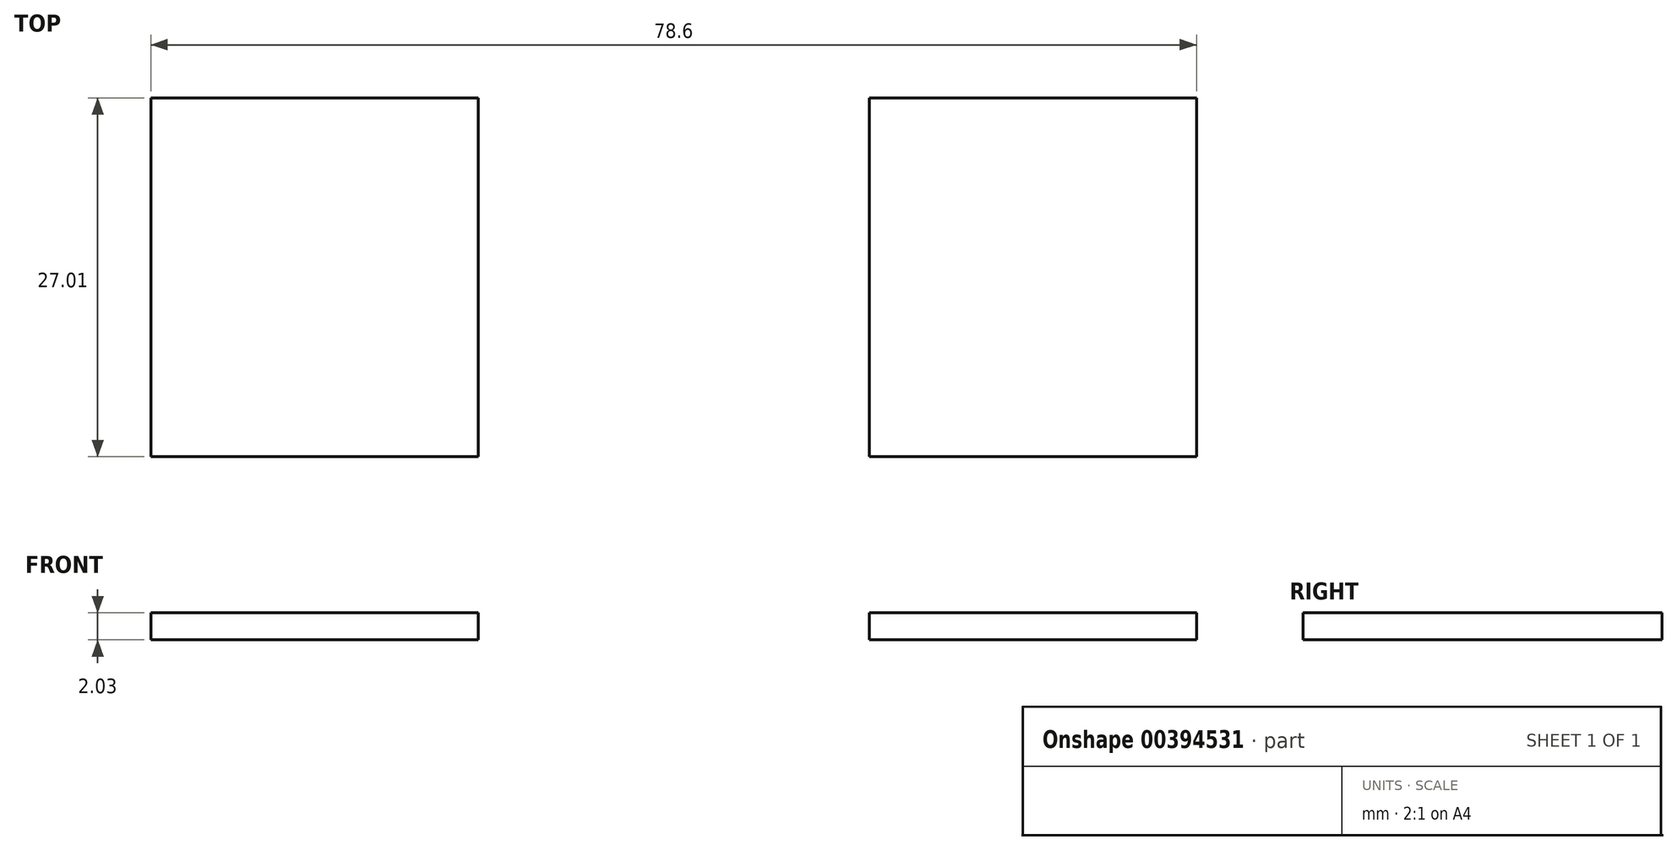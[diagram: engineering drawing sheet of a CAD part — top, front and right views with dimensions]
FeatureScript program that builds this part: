
annotation { "Feature Type Name" : "Feature", "Feature Type Description" : "" }
export const myFeature = defineFeature(function(context is Context, id is Id, definition is map)
    precondition{}
    {
        {
            var Q0;
            Q0=qCreatedBy(makeId("Top.planeOp"),FACE);
            var sketch = newSketch(context, id + "F0", { "sketchPlane" : qUnion([Q0])});
            skLineSegment(sketch, "E0.bottom", {"start": v(-39.3, 27) * mm, "end": v(-14.71, 27) * mm});
            skLineSegment(sketch, "E0.top", {"start": v(-39.3, 0) * mm, "end": v(-14.71, 0) * mm});
            skLineSegment(sketch, "E0.left", {"start": v(-39.3, 27) * mm, "end": v(-39.3, 0) * mm});
            skLineSegment(sketch, "E0.right", {"start": v(-14.71, 27) * mm, "end": v(-14.71, 0) * mm});
            skLineSegment(sketch, "E1.MirrorCS", {"start": v(14.71, 27) * mm, "end": v(14.71, 0) * mm});
            skLineSegment(sketch, "E2.MirrorCS", {"start": v(39.3, 27) * mm, "end": v(39.3, 0) * mm});
            skLineSegment(sketch, "E3.MirrorCS", {"start": v(39.3, 0) * mm, "end": v(14.71, 0) * mm});
            skLineSegment(sketch, "E4.MirrorCS", {"start": v(39.3, 27) * mm, "end": v(14.71, 27) * mm});
            skLineSegment(sketch, "E5.bottom", {"start": v(-8.26, 0.2) * mm, "end": v(9.47, 0.2) * mm});
            skLineSegment(sketch, "E5.top", {"start": v(-8.26, -13.9) * mm, "end": v(9.47, -13.9) * mm});
            skLineSegment(sketch, "E5.left", {"start": v(-8.26, 0.2) * mm, "end": v(-8.26, -13.9) * mm});
            skLineSegment(sketch, "E5.right", {"start": v(9.47, 0.2) * mm, "end": v(9.47, -13.9) * mm});
            skSolve(sketch);
        }
        {
            var Q0;
            Q0=makeQuery(id+"F0.imprint","IMPRINT",FACE,{"disambiguationData":[TD([[makeQuery(id+"F0.imprint","IMPRINT",EDGE,{"derivedFrom":sQuery(id+"F0.wireOp",EDGE,"E0.bottom")}),-1.0]])]});
            var Q1;
            Q1=makeQuery(id+"F0.imprint","IMPRINT",FACE,{"disambiguationData":[TD([[makeQuery(id+"F0.imprint","IMPRINT",EDGE,{"derivedFrom":sQuery(id+"F0.wireOp",EDGE,"E1.MirrorCS")}),1.0]])]});
            extrude(context, id + "F1", {"entities" : qUnion([Q0, Q1]), "depth" : 2.03 * mm});
        }
        {
            var Q0;
            Q0=qCreatedBy(makeId("Top.planeOp"),FACE);
            var sketch = newSketch(context, id + "F2", { "sketchPlane" : qUnion([Q0])});
            skLineSegment(sketch, "E6.bottom", {"start": v(-5.84, -2.22) * mm, "end": v(6.45, -2.22) * mm});
            skLineSegment(sketch, "E6.top", {"start": v(-5.84, -11.08) * mm, "end": v(6.45, -11.08) * mm});
            skLineSegment(sketch, "E6.left", {"start": v(-5.84, -2.22) * mm, "end": v(-5.84, -11.08) * mm});
            skLineSegment(sketch, "E6.right", {"start": v(6.45, -2.22) * mm, "end": v(6.45, -11.08) * mm});
            skSolve(sketch);
        }
    });
